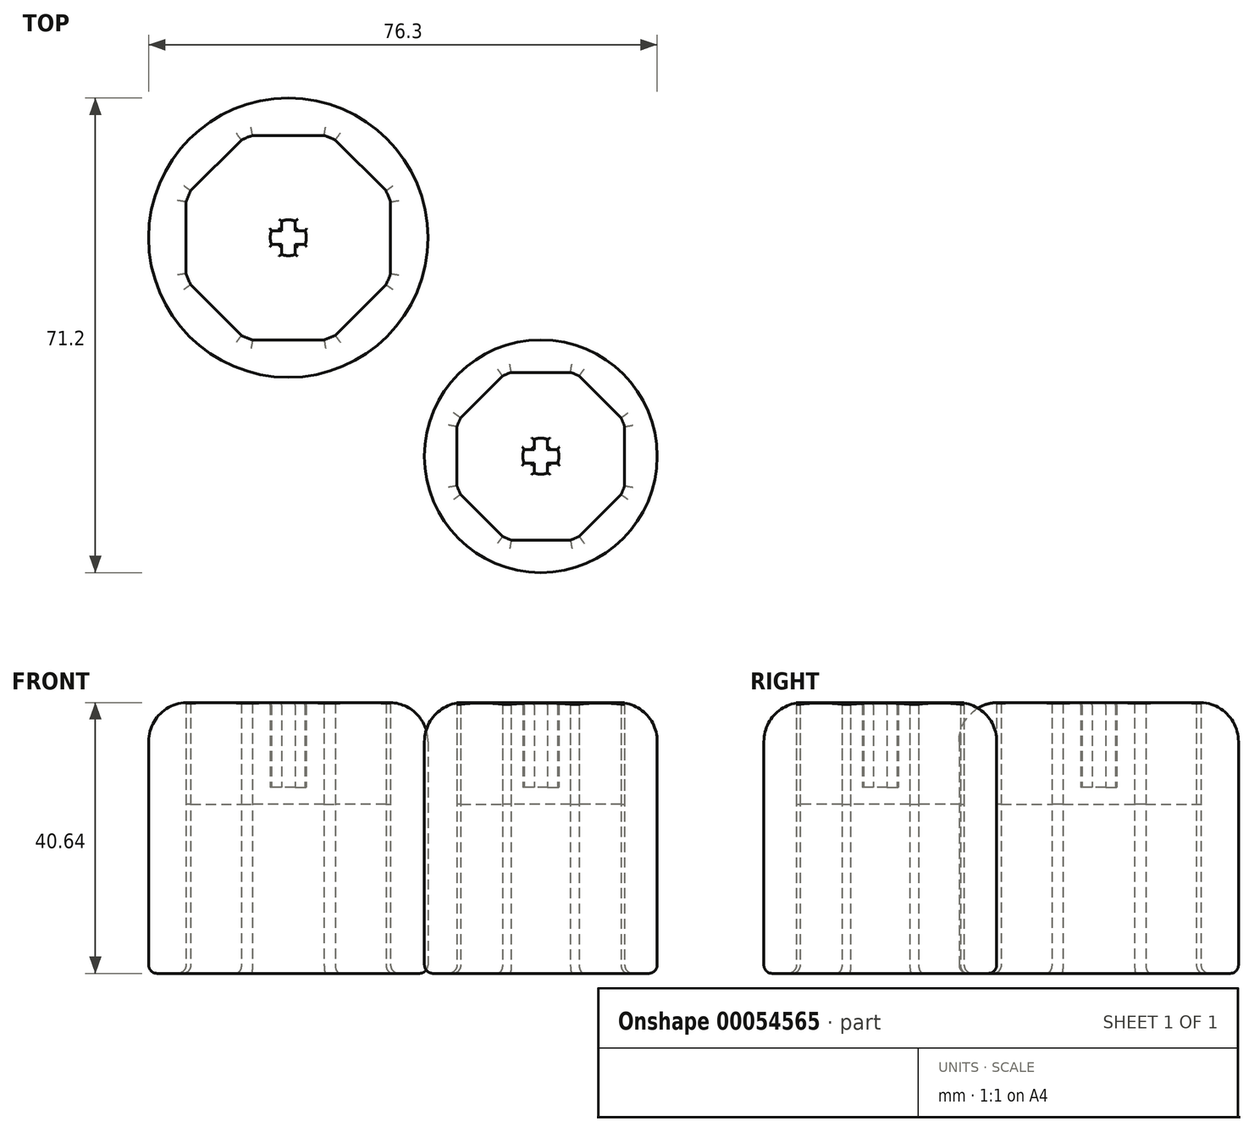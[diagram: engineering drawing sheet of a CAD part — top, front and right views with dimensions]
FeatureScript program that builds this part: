
annotation { "Feature Type Name" : "Feature", "Feature Type Description" : "" }
export const myFeature = defineFeature(function(context is Context, id is Id, definition is map)
    precondition{}
    {
        {
            var Q0;
            Q0=qCreatedBy(makeId("Top.planeOp"),FACE);
            var sketch = newSketch(context, id + "F0", { "sketchPlane" : qUnion([Q0])});
            skCircle(sketch, "E0", {"center": v(0, 0) * mm, "radius": 17.46 * mm});
            skArc(sketch, "E1", {"start": v(-12.03, 5.75) * mm, "mid": v(-12.32, 5.1) * mm, "end": v(-12.57, 4.44) * mm});
            skLineSegment(sketch, "E2", {"start": v(-4.44, 12.57) * mm, "end": v(4.44, 12.57) * mm});
            skLineSegment(sketch, "E3.1.0", {"start": v(-12.03, 5.75) * mm, "end": v(-5.75, 12.03) * mm});
            skLineSegment(sketch, "E3.2.0", {"start": v(-12.57, -4.44) * mm, "end": v(-12.57, 4.44) * mm});
            skLineSegment(sketch, "E3.3.0", {"start": v(-5.75, -12.03) * mm, "end": v(-12.03, -5.75) * mm});
            skLineSegment(sketch, "E3.4.0", {"start": v(4.44, -12.57) * mm, "end": v(-4.44, -12.57) * mm});
            skLineSegment(sketch, "E3.5.0", {"start": v(12.03, -5.75) * mm, "end": v(5.75, -12.03) * mm});
            skLineSegment(sketch, "E3.6.0", {"start": v(12.57, 4.44) * mm, "end": v(12.57, -4.44) * mm});
            skLineSegment(sketch, "E3.7.0", {"start": v(5.75, 12.03) * mm, "end": v(12.03, 5.75) * mm});
            skArc(sketch, "E4.trimOffspring", {"start": v(-12.57, -4.44) * mm, "mid": v(-12.32, -5.1) * mm, "end": v(-12.03, -5.75) * mm});
            skArc(sketch, "E5.trimOffspring", {"start": v(-5.75, -12.03) * mm, "mid": v(-5.1, -12.32) * mm, "end": v(-4.44, -12.57) * mm});
            skArc(sketch, "E6.trimOffspring", {"start": v(4.44, -12.57) * mm, "mid": v(5.1, -12.32) * mm, "end": v(5.75, -12.03) * mm});
            skArc(sketch, "E7.trimOffspring", {"start": v(12.03, -5.75) * mm, "mid": v(12.32, -5.1) * mm, "end": v(12.57, -4.44) * mm});
            skArc(sketch, "E8.trimOffspring", {"start": v(12.57, 4.44) * mm, "mid": v(12.32, 5.1) * mm, "end": v(12.03, 5.75) * mm});
            skArc(sketch, "E9.trimOffspring", {"start": v(5.75, 12.03) * mm, "mid": v(5.1, 12.32) * mm, "end": v(4.44, 12.57) * mm});
            skArc(sketch, "E10.trimOffspring", {"start": v(-4.44, 12.57) * mm, "mid": v(-5.1, 12.32) * mm, "end": v(-5.75, 12.03) * mm});
            skPoint(sketch, "E11.end.orphan", {"position": v(0, 12.57) * mm});
            skLineSegment(sketch, "E12", {"start": v(1.01, 1.01) * mm, "end": v(1.01, 2.5) * mm});
            skLineSegment(sketch, "E13", {"start": v(-1.01, 1.01) * mm, "end": v(-1.01, 2.5) * mm});
            skLineSegment(sketch, "E14", {"start": v(-1.01, -1.01) * mm, "end": v(-1.01, -2.5) * mm});
            skArc(sketch, "E15", {"start": v(1.01, 2.5) * mm, "mid": v(0, 2.7) * mm, "end": v(-1.01, 2.5) * mm});
            skArc(sketch, "E16.trimOffspring", {"start": v(2.5, -1.01) * mm, "mid": v(2.7, 0) * mm, "end": v(2.5, 1.01) * mm});
            skCircle(sketch, "E17", {"center": v(0, 0) * mm, "radius": 6.35 * mm});
            skArc(sketch, "E18.trimOffspring", {"start": v(-1.01, -2.5) * mm, "mid": v(0, -2.7) * mm, "end": v(1.01, -2.5) * mm});
            skArc(sketch, "E19.trimOffspring", {"start": v(-2.5, 1.01) * mm, "mid": v(-2.7, 0) * mm, "end": v(-2.5, -1.01) * mm});
            skLineSegment(sketch, "E20", {"start": v(1.01, -1.01) * mm, "end": v(1.01, -2.5) * mm});
            skLineSegment(sketch, "E21", {"start": v(1.01, -1.01) * mm, "end": v(2.5, -1.01) * mm});
            skLineSegment(sketch, "E22", {"start": v(-1.01, -1.01) * mm, "end": v(-2.5, -1.01) * mm});
            skLineSegment(sketch, "E23", {"start": v(-1.01, 1.01) * mm, "end": v(-2.5, 1.01) * mm});
            skLineSegment(sketch, "E24", {"start": v(1.01, 1.01) * mm, "end": v(2.5, 1.01) * mm});
            skLineSegment(sketch, "E25.6.0", {"start": v(-22.54, 38.16) * mm, "end": v(-22.54, 27.4) * mm});
            skLineSegment(sketch, "E25.4.0", {"start": v(-32.51, 17.44) * mm, "end": v(-43.26, 17.44) * mm});
            skLineSegment(sketch, "E25.3.0", {"start": v(-44.93, 18.13) * mm, "end": v(-52.54, 25.73) * mm});
            skLineSegment(sketch, "E25.7.0", {"start": v(-30.84, 47.43) * mm, "end": v(-23.24, 39.83) * mm});
            skLineSegment(sketch, "E25.5.0", {"start": v(-23.24, 25.73) * mm, "end": v(-30.84, 18.13) * mm});
            skLineSegment(sketch, "E25.2.0", {"start": v(-53.23, 27.4) * mm, "end": v(-53.23, 38.16) * mm});
            skLineSegment(sketch, "E25.1.0", {"start": v(-52.54, 39.83) * mm, "end": v(-44.93, 47.43) * mm});
            skLineSegment(sketch, "E26", {"start": v(-43.26, 48.12) * mm, "end": v(-32.51, 48.12) * mm});
            skArc(sketch, "E27.trimOffspring", {"start": v(-32.51, 17.44) * mm, "mid": v(-31.67, 17.76) * mm, "end": v(-30.84, 18.13) * mm});
            skArc(sketch, "E28.trimOffspring", {"start": v(-30.84, 47.43) * mm, "mid": v(-31.67, 47.8) * mm, "end": v(-32.51, 48.12) * mm});
            skArc(sketch, "E29.trimOffspring", {"start": v(-43.26, 48.12) * mm, "mid": v(-44.1, 47.8) * mm, "end": v(-44.93, 47.43) * mm});
            skArc(sketch, "E30", {"start": v(-52.54, 39.83) * mm, "mid": v(-52.9, 39) * mm, "end": v(-53.23, 38.16) * mm});
            skArc(sketch, "E31.trimOffspring", {"start": v(-22.54, 38.16) * mm, "mid": v(-22.87, 39) * mm, "end": v(-23.24, 39.83) * mm});
            skArc(sketch, "E32.trimOffspring", {"start": v(-53.23, 27.4) * mm, "mid": v(-52.9, 26.56) * mm, "end": v(-52.54, 25.73) * mm});
            skArc(sketch, "E33.trimOffspring", {"start": v(-44.93, 18.13) * mm, "mid": v(-44.1, 17.76) * mm, "end": v(-43.26, 17.44) * mm});
            skArc(sketch, "E34.trimOffspring", {"start": v(-23.24, 25.73) * mm, "mid": v(-22.87, 26.56) * mm, "end": v(-22.54, 27.4) * mm});
            skCircle(sketch, "E35", {"center": v(-37.89, 32.78) * mm, "radius": 20.96 * mm});
            skLineSegment(sketch, "E36", {"start": v(-38.9, 31.77) * mm, "end": v(-38.9, 30.28) * mm});
            skLineSegment(sketch, "E37", {"start": v(-36.87, 31.77) * mm, "end": v(-35.38, 31.77) * mm});
            skLineSegment(sketch, "E38", {"start": v(-36.87, 33.8) * mm, "end": v(-36.87, 35.28) * mm});
            skLineSegment(sketch, "E39", {"start": v(-38.9, 31.77) * mm, "end": v(-40.39, 31.77) * mm});
            skArc(sketch, "E40.trimOffspring", {"start": v(-35.38, 31.77) * mm, "mid": v(-35.19, 32.78) * mm, "end": v(-35.38, 33.8) * mm});
            skLineSegment(sketch, "E41", {"start": v(-38.9, 33.8) * mm, "end": v(-40.39, 33.8) * mm});
            skArc(sketch, "E42.trimOffspring", {"start": v(-40.39, 33.8) * mm, "mid": v(-40.59, 32.78) * mm, "end": v(-40.39, 31.77) * mm});
            skLineSegment(sketch, "E43", {"start": v(-38.9, 33.8) * mm, "end": v(-38.9, 35.28) * mm});
            skLineSegment(sketch, "E44", {"start": v(-36.87, 31.77) * mm, "end": v(-36.87, 30.28) * mm});
            skArc(sketch, "E45.trimOffspring", {"start": v(-38.9, 30.28) * mm, "mid": v(-37.89, 30.08) * mm, "end": v(-36.87, 30.28) * mm});
            skArc(sketch, "E46", {"start": v(-36.87, 35.28) * mm, "mid": v(-37.89, 35.48) * mm, "end": v(-38.9, 35.28) * mm});
            skLineSegment(sketch, "E47", {"start": v(-36.87, 33.8) * mm, "end": v(-35.38, 33.8) * mm});
            skCircle(sketch, "E48", {"center": v(-37.89, 32.78) * mm, "radius": 6.35 * mm});
            skSolve(sketch);
        }
        {
            var Q0;
            Q0=makeQuery(id+"F0.imprint","IMPRINT",FACE,{"disambiguationData":[TD([[makeQuery(id+"F0.imprint","IMPRINT",EDGE,{"derivedFrom":sQuery(id+"F0.wireOp",EDGE,"E12")}),1.0]])]});
            var Q1;
            Q1=makeQuery(id+"F0.imprint","IMPRINT",FACE,{"disambiguationData":[TD([[makeQuery(id+"F0.imprint","IMPRINT",EDGE,{"derivedFrom":sQuery(id+"F0.wireOp",EDGE,"E36")}),1.0]])]});
            extrude(context, id + "F1", {"entities" : qUnion([Q0, Q1]), "depth" : 27.94 * mm, "hasSecondDirection" : true, "secondDirectionOppositeDirection" : false, "secondDirectionDepth" : 25.4 * mm});
        }
        {
            var Q0;
            Q0=makeQuery(id+"F0.imprint","IMPRINT",FACE,{"disambiguationData":[TD([[makeQuery(id+"F0.imprint","IMPRINT",EDGE,{"derivedFrom":sQuery(id+"F0.wireOp",EDGE,"E12")}),-1.0]])]});
            var Q1;
            Q1=makeQuery(id+"F0.imprint","IMPRINT",FACE,{"disambiguationData":[TD([[makeQuery(id+"F0.imprint","IMPRINT",EDGE,{"derivedFrom":sQuery(id+"F0.wireOp",EDGE,"E36")}),-1.0]])]});
            extrude(context, id + "F2", {"entities" : qUnion([Q0, Q1]), "operationType" : NewBodyOperationType.ADD, "depth" : 40.64 * mm, "hasSecondDirection" : true, "secondDirectionOppositeDirection" : false, "secondDirectionDepth" : 25.4 * mm});
        }
        {
            var Q0;
            Q0=makeQuery(id+"F0.imprint","IMPRINT",FACE,{"disambiguationData":[TD([[makeQuery(id+"F0.imprint","IMPRINT",EDGE,{"derivedFrom":sQuery(id+"F0.wireOp",EDGE,"E1")}),1.0]])]});
            var Q1;
            Q1=makeQuery(id+"F0.imprint","IMPRINT",FACE,{"disambiguationData":[TD([[makeQuery(id+"F0.imprint","IMPRINT",EDGE,{"derivedFrom":sQuery(id+"F0.wireOp",EDGE,"E25.6.0")}),-1.0]])]});
            extrude(context, id + "F3", {"entities" : qUnion([Q0, Q1]), "operationType" : NewBodyOperationType.ADD, "depth" : 40.64 * mm, "hasSecondDirection" : true, "secondDirectionOppositeDirection" : false, "secondDirectionDepth" : 25.4 * mm});
        }
        {
            var Q0;
            Q0=makeQuery(id+"F0.imprint","IMPRINT",FACE,{"disambiguationData":[TD([[makeQuery(id+"F0.imprint","IMPRINT",EDGE,{"derivedFrom":sQuery(id+"F0.wireOp",EDGE,"E0")}),1.0]])]});
            var Q1;
            Q1=makeQuery(id+"F0.imprint","IMPRINT",FACE,{"disambiguationData":[TD([[makeQuery(id+"F0.imprint","IMPRINT",EDGE,{"derivedFrom":sQuery(id+"F0.wireOp",EDGE,"E25.6.0")}),1.0]])]});
            extrude(context, id + "F4", {"entities" : qUnion([Q0, Q1]), "depth" : 40.64 * mm});
        }
        {
            var Q0;
            Q0=makeQuery(id+"F2.opExtrude","CAP_EDGE",EDGE,{"disambiguationData":[OSD([sQuery(id+"F0.wireOp",EDGE,"E20")])],"isStart":false});
            var Q1;
            Q1=makeQuery(id+"F2.opExtrude","CAP_EDGE",EDGE,{"disambiguationData":[OSD([sQuery(id+"F0.wireOp",EDGE,"E16.trimOffspring")])],"isStart":false});
            var Q2;
            Q2=makeQuery(id+"F2.opExtrude","CAP_EDGE",EDGE,{"disambiguationData":[OSD([sQuery(id+"F0.wireOp",EDGE,"E24")])],"isStart":false});
            var Q3;
            Q3=makeQuery(id+"F2.opExtrude","CAP_EDGE",EDGE,{"disambiguationData":[OSD([sQuery(id+"F0.wireOp",EDGE,"E21")])],"isStart":false});
            var Q4;
            Q4=makeQuery(id+"F2.opExtrude","CAP_EDGE",EDGE,{"disambiguationData":[OSD([sQuery(id+"F0.wireOp",EDGE,"E18.trimOffspring")])],"isStart":false});
            var Q5;
            Q5=makeQuery(id+"F2.opExtrude","CAP_EDGE",EDGE,{"disambiguationData":[OSD([sQuery(id+"F0.wireOp",EDGE,"E14")])],"isStart":false});
            var Q6;
            Q6=makeQuery(id+"F2.opExtrude","CAP_EDGE",EDGE,{"disambiguationData":[OSD([sQuery(id+"F0.wireOp",EDGE,"E19.trimOffspring")])],"isStart":false});
            var Q7;
            Q7=makeQuery(id+"F2.opExtrude","CAP_EDGE",EDGE,{"disambiguationData":[OSD([sQuery(id+"F0.wireOp",EDGE,"E22")])],"isStart":false});
            var Q8;
            Q8=makeQuery(id+"F2.opExtrude","CAP_EDGE",EDGE,{"disambiguationData":[OSD([sQuery(id+"F0.wireOp",EDGE,"E23")])],"isStart":false});
            var Q9;
            Q9=makeQuery(id+"F2.opExtrude","CAP_EDGE",EDGE,{"disambiguationData":[OSD([sQuery(id+"F0.wireOp",EDGE,"E13")])],"isStart":false});
            var Q10;
            Q10=makeQuery(id+"F2.opExtrude","CAP_EDGE",EDGE,{"disambiguationData":[OSD([sQuery(id+"F0.wireOp",EDGE,"E15")])],"isStart":false});
            var Q11;
            Q11=makeQuery(id+"F2.opExtrude","CAP_EDGE",EDGE,{"disambiguationData":[OSD([sQuery(id+"F0.wireOp",EDGE,"E12")])],"isStart":false});
            var Q12;
            Q12=makeQuery(id+"F2.opExtrude","CAP_EDGE",EDGE,{"disambiguationData":[OSD([sQuery(id+"F0.wireOp",EDGE,"E47")])],"isStart":false});
            var Q13;
            Q13=makeQuery(id+"F2.opExtrude","CAP_EDGE",EDGE,{"disambiguationData":[OSD([sQuery(id+"F0.wireOp",EDGE,"E40.trimOffspring")])],"isStart":false});
            var Q14;
            Q14=makeQuery(id+"F2.opExtrude","CAP_EDGE",EDGE,{"disambiguationData":[OSD([sQuery(id+"F0.wireOp",EDGE,"E44")])],"isStart":false});
            var Q15;
            Q15=makeQuery(id+"F2.opExtrude","CAP_EDGE",EDGE,{"disambiguationData":[OSD([sQuery(id+"F0.wireOp",EDGE,"E38")])],"isStart":false});
            var Q16;
            Q16=makeQuery(id+"F2.opExtrude","CAP_EDGE",EDGE,{"disambiguationData":[OSD([sQuery(id+"F0.wireOp",EDGE,"E46")])],"isStart":false});
            var Q17;
            Q17=makeQuery(id+"F2.opExtrude","CAP_EDGE",EDGE,{"disambiguationData":[OSD([sQuery(id+"F0.wireOp",EDGE,"E37")])],"isStart":false});
            var Q18;
            Q18=makeQuery(id+"F2.opExtrude","CAP_EDGE",EDGE,{"disambiguationData":[OSD([sQuery(id+"F0.wireOp",EDGE,"E41")])],"isStart":false});
            var Q19;
            Q19=makeQuery(id+"F2.opExtrude","CAP_EDGE",EDGE,{"disambiguationData":[OSD([sQuery(id+"F0.wireOp",EDGE,"E43")])],"isStart":false});
            var Q20;
            Q20=makeQuery(id+"F2.opExtrude","CAP_EDGE",EDGE,{"disambiguationData":[OSD([sQuery(id+"F0.wireOp",EDGE,"E39")])],"isStart":false});
            var Q21;
            Q21=makeQuery(id+"F2.opExtrude","CAP_EDGE",EDGE,{"disambiguationData":[OSD([sQuery(id+"F0.wireOp",EDGE,"E42.trimOffspring")])],"isStart":false});
            var Q22;
            Q22=makeQuery(id+"F2.opExtrude","CAP_EDGE",EDGE,{"disambiguationData":[OSD([sQuery(id+"F0.wireOp",EDGE,"E36")])],"isStart":false});
            var Q23;
            Q23=makeQuery(id+"F2.opExtrude","CAP_EDGE",EDGE,{"disambiguationData":[OSD([sQuery(id+"F0.wireOp",EDGE,"E45.trimOffspring")])],"isStart":false});
            fillet(context, id + "F5", {"entities" : qUnion([Q0, Q1, Q2, Q3, Q4, Q5, Q6, Q7, Q8, Q9, Q10, Q11, Q12, Q13, Q14, Q15, Q16, Q17, Q18, Q19, Q20, Q21, Q22, Q23]), "radius" : 0.38 * mm, "tangentPropagation" : true, "allowEdgeOverflow" : false});
        }
        {
            var Q0;
            Q0=makeQuery(id+"F4.opExtrude","CAP_EDGE",EDGE,{"disambiguationData":[OSD([sQuery(id+"F0.wireOp",EDGE,"E0")])],"isStart":false});
            var Q1;
            Q1=makeQuery(id+"F4.opExtrude","CAP_EDGE",EDGE,{"disambiguationData":[OSD([sQuery(id+"F0.wireOp",EDGE,"E35")])],"isStart":false});
            fillet(context, id + "F6", {"entities" : qUnion([Q0, Q1]), "radius" : 5.84 * mm, "tangentPropagation" : true, "allowEdgeOverflow" : false});
        }
        {
            var Q0;
            Q0=makeQuery(id+"F4.opExtrude","CAP_EDGE",EDGE,{"disambiguationData":[OSD([sQuery(id+"F0.wireOp",EDGE,"E0")])],"isStart":true});
            var Q1;
            Q1=makeQuery(id+"F4.opExtrude","CAP_EDGE",EDGE,{"disambiguationData":[OSD([sQuery(id+"F0.wireOp",EDGE,"E3.3.0")])],"isStart":true});
            var Q2;
            Q2=makeQuery(id+"F4.opExtrude","CAP_EDGE",EDGE,{"disambiguationData":[OSD([sQuery(id+"F0.wireOp",EDGE,"E3.2.0")])],"isStart":true});
            var Q3;
            Q3=makeQuery(id+"F4.opExtrude","CAP_EDGE",EDGE,{"disambiguationData":[OSD([sQuery(id+"F0.wireOp",EDGE,"E4.trimOffspring")])],"isStart":true});
            var Q4;
            Q4=makeQuery(id+"F4.opExtrude","CAP_EDGE",EDGE,{"disambiguationData":[OSD([sQuery(id+"F0.wireOp",EDGE,"E5.trimOffspring")])],"isStart":true});
            var Q5;
            Q5=makeQuery(id+"F4.opExtrude","CAP_EDGE",EDGE,{"disambiguationData":[OSD([sQuery(id+"F0.wireOp",EDGE,"E3.4.0")])],"isStart":true});
            var Q6;
            Q6=makeQuery(id+"F4.opExtrude","CAP_EDGE",EDGE,{"disambiguationData":[OSD([sQuery(id+"F0.wireOp",EDGE,"E6.trimOffspring")])],"isStart":true});
            var Q7;
            Q7=makeQuery(id+"F4.opExtrude","CAP_EDGE",EDGE,{"disambiguationData":[OSD([sQuery(id+"F0.wireOp",EDGE,"E3.5.0")])],"isStart":true});
            var Q8;
            Q8=makeQuery(id+"F4.opExtrude","CAP_EDGE",EDGE,{"disambiguationData":[OSD([sQuery(id+"F0.wireOp",EDGE,"E3.1.0")])],"isStart":true});
            var Q9;
            Q9=makeQuery(id+"F4.opExtrude","CAP_EDGE",EDGE,{"disambiguationData":[OSD([sQuery(id+"F0.wireOp",EDGE,"E1")])],"isStart":true});
            var Q10;
            Q10=makeQuery(id+"F4.opExtrude","CAP_EDGE",EDGE,{"disambiguationData":[OSD([sQuery(id+"F0.wireOp",EDGE,"E10.trimOffspring")])],"isStart":true});
            var Q11;
            Q11=makeQuery(id+"F4.opExtrude","CAP_EDGE",EDGE,{"disambiguationData":[OSD([sQuery(id+"F0.wireOp",EDGE,"E2")])],"isStart":true});
            var Q12;
            Q12=makeQuery(id+"F4.opExtrude","CAP_EDGE",EDGE,{"disambiguationData":[OSD([sQuery(id+"F0.wireOp",EDGE,"E9.trimOffspring")])],"isStart":true});
            var Q13;
            Q13=makeQuery(id+"F4.opExtrude","CAP_EDGE",EDGE,{"disambiguationData":[OSD([sQuery(id+"F0.wireOp",EDGE,"E3.7.0")])],"isStart":true});
            var Q14;
            Q14=makeQuery(id+"F4.opExtrude","CAP_EDGE",EDGE,{"disambiguationData":[OSD([sQuery(id+"F0.wireOp",EDGE,"E8.trimOffspring")])],"isStart":true});
            var Q15;
            Q15=makeQuery(id+"F4.opExtrude","CAP_EDGE",EDGE,{"disambiguationData":[OSD([sQuery(id+"F0.wireOp",EDGE,"E3.6.0")])],"isStart":true});
            var Q16;
            Q16=makeQuery(id+"F4.opExtrude","CAP_EDGE",EDGE,{"disambiguationData":[OSD([sQuery(id+"F0.wireOp",EDGE,"E7.trimOffspring")])],"isStart":true});
            var Q17;
            Q17=makeQuery(id+"F4.opExtrude","CAP_EDGE",EDGE,{"disambiguationData":[OSD([sQuery(id+"F0.wireOp",EDGE,"E35")])],"isStart":true});
            var Q18;
            Q18=makeQuery(id+"F4.opExtrude","CAP_EDGE",EDGE,{"disambiguationData":[OSD([sQuery(id+"F0.wireOp",EDGE,"E25.4.0")])],"isStart":true});
            var Q19;
            Q19=makeQuery(id+"F4.opExtrude","CAP_EDGE",EDGE,{"disambiguationData":[OSD([sQuery(id+"F0.wireOp",EDGE,"E25.3.0")])],"isStart":true});
            var Q20;
            Q20=makeQuery(id+"F4.opExtrude","CAP_EDGE",EDGE,{"disambiguationData":[OSD([sQuery(id+"F0.wireOp",EDGE,"E33.trimOffspring")])],"isStart":true});
            var Q21;
            Q21=makeQuery(id+"F4.opExtrude","CAP_EDGE",EDGE,{"disambiguationData":[OSD([sQuery(id+"F0.wireOp",EDGE,"E27.trimOffspring")])],"isStart":true});
            var Q22;
            Q22=makeQuery(id+"F4.opExtrude","CAP_EDGE",EDGE,{"disambiguationData":[OSD([sQuery(id+"F0.wireOp",EDGE,"E25.5.0")])],"isStart":true});
            var Q23;
            Q23=makeQuery(id+"F4.opExtrude","CAP_EDGE",EDGE,{"disambiguationData":[OSD([sQuery(id+"F0.wireOp",EDGE,"E34.trimOffspring")])],"isStart":true});
            var Q24;
            Q24=makeQuery(id+"F4.opExtrude","CAP_EDGE",EDGE,{"disambiguationData":[OSD([sQuery(id+"F0.wireOp",EDGE,"E25.6.0")])],"isStart":true});
            var Q25;
            Q25=makeQuery(id+"F4.opExtrude","CAP_EDGE",EDGE,{"disambiguationData":[OSD([sQuery(id+"F0.wireOp",EDGE,"E31.trimOffspring")])],"isStart":true});
            var Q26;
            Q26=makeQuery(id+"F4.opExtrude","CAP_EDGE",EDGE,{"disambiguationData":[OSD([sQuery(id+"F0.wireOp",EDGE,"E25.7.0")])],"isStart":true});
            var Q27;
            Q27=makeQuery(id+"F4.opExtrude","CAP_EDGE",EDGE,{"disambiguationData":[OSD([sQuery(id+"F0.wireOp",EDGE,"E32.trimOffspring")])],"isStart":true});
            var Q28;
            Q28=makeQuery(id+"F4.opExtrude","CAP_EDGE",EDGE,{"disambiguationData":[OSD([sQuery(id+"F0.wireOp",EDGE,"E25.2.0")])],"isStart":true});
            var Q29;
            Q29=makeQuery(id+"F4.opExtrude","CAP_EDGE",EDGE,{"disambiguationData":[OSD([sQuery(id+"F0.wireOp",EDGE,"E30")])],"isStart":true});
            var Q30;
            Q30=makeQuery(id+"F4.opExtrude","CAP_EDGE",EDGE,{"disambiguationData":[OSD([sQuery(id+"F0.wireOp",EDGE,"E25.1.0")])],"isStart":true});
            var Q31;
            Q31=makeQuery(id+"F4.opExtrude","CAP_EDGE",EDGE,{"disambiguationData":[OSD([sQuery(id+"F0.wireOp",EDGE,"E29.trimOffspring")])],"isStart":true});
            var Q32;
            Q32=makeQuery(id+"F4.opExtrude","CAP_EDGE",EDGE,{"disambiguationData":[OSD([sQuery(id+"F0.wireOp",EDGE,"E26")])],"isStart":true});
            var Q33;
            Q33=makeQuery(id+"F4.opExtrude","CAP_EDGE",EDGE,{"disambiguationData":[OSD([sQuery(id+"F0.wireOp",EDGE,"E28.trimOffspring")])],"isStart":true});
            fillet(context, id + "F7", {"entities" : qUnion([Q0, Q1, Q2, Q3, Q4, Q5, Q6, Q7, Q8, Q9, Q10, Q11, Q12, Q13, Q14, Q15, Q16, Q17, Q18, Q19, Q20, Q21, Q22, Q23, Q24, Q25, Q26, Q27, Q28, Q29, Q30, Q31, Q32, Q33]), "radius" : 1.27 * mm, "tangentPropagation" : true, "allowEdgeOverflow" : false});
        }
    });
